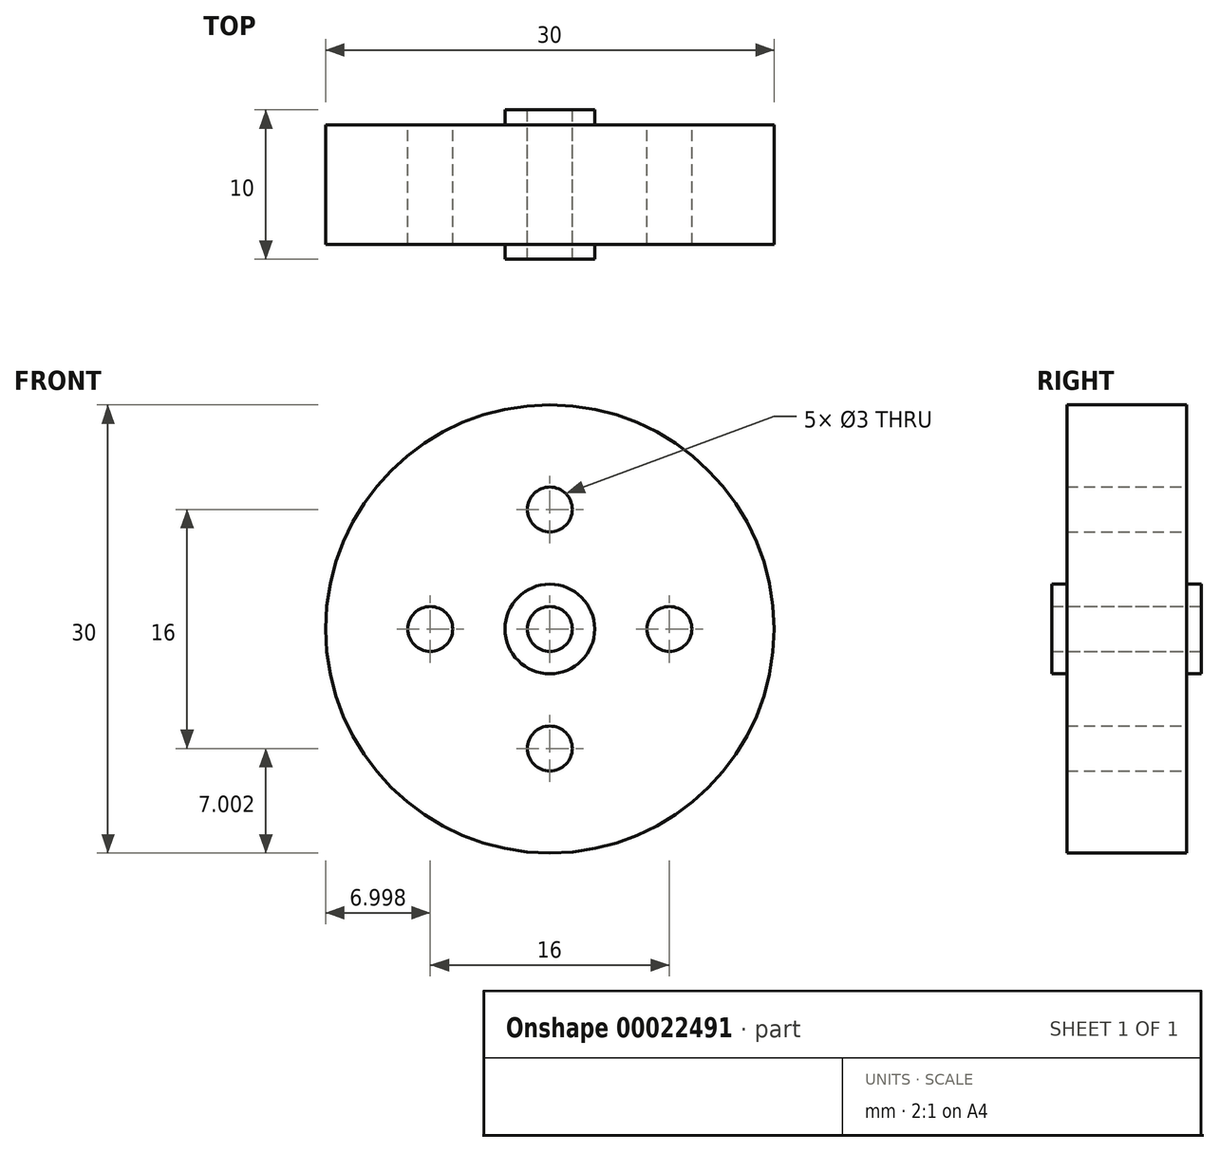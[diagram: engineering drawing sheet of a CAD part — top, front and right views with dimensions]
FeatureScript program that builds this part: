
annotation { "Feature Type Name" : "Feature", "Feature Type Description" : "" }
export const myFeature = defineFeature(function(context is Context, id is Id, definition is map)
    precondition{}
    {
        {
            var Q0;
            Q0=qCreatedBy(makeId("Front.planeOp"),FACE);
            var sketch = newSketch(context, id + "F0", { "sketchPlane" : qUnion([Q0])});
            skCircle(sketch, "E0", {"center": v(-18.25, 12.61) * mm, "radius": 15 * mm});
            skCircle(sketch, "E1", {"center": v(-18.25, 12.61) * mm, "radius": 1.5 * mm});
            skCircle(sketch, "E2", {"center": v(-18.25, 12.61) * mm, "radius": 3.5 * mm});
            skLineSegment(sketch, "E3", {"start": v(-18.25, 12.61) * mm, "end": v(-18.25, 27.61) * mm});
            skCircle(sketch, "E4", {"center": v(-18.25, 20.61) * mm, "radius": 1.5 * mm});
            skCircle(sketch, "E5.1.0", {"center": v(-26.25, 12.61) * mm, "radius": 1.5 * mm});
            skCircle(sketch, "E5.2.0", {"center": v(-18.25, 4.61) * mm, "radius": 1.5 * mm});
            skCircle(sketch, "E5.3.0", {"center": v(-10.25, 12.61) * mm, "radius": 1.5 * mm});
            skSolve(sketch);
        }
        {
            var Q0;
            Q0=makeQuery(id+"F0.imprint","IMPRINT",FACE,{"disambiguationData":[TD([[makeQuery(id+"F0.imprint","IMPRINT",EDGE,{"derivedFrom":sQuery(id+"F0.wireOp",EDGE,"E0")}),1.0]])]});
            var Q1;
            Q1=makeQuery(id+"F0.imprint","IMPRINT",FACE,{"disambiguationData":[TD([[makeQuery(id+"F0.imprint","IMPRINT",EDGE,{"derivedFrom":sQuery(id+"F0.wireOp",EDGE,"E1")}),-1.0]])]});
            extrude(context, id + "F1", {"entities" : qUnion([Q0, Q1]), "depth" : 8 * mm});
        }
        {
            var Q0;
            Q0=makeQuery(id+"F1.opExtrude","CAP_FACE",FACE,{"disambiguationData":[OSD([sQuery(id+"F0.wireOp",EDGE,"E0"),sQuery(id+"F0.wireOp",EDGE,"E1")])],"isStart":true});
            var sketch = newSketch(context, id + "F2", { "sketchPlane" : qUnion([Q0])});
            skCircle(sketch, "E6", {"center": v(18.25, 12.61) * mm, "radius": 3 * mm});
            skSolve(sketch);
        }
        {
            var Q0;
            Q0=makeQuery(id+"F2.imprint","IMPRINT",FACE,{"disambiguationData":[TD([[makeQuery(id+"F2.imprint","IMPRINT",EDGE,{"derivedFrom":sQuery(id+"F2.wireOp",EDGE,"E6")}),1.0]])]});
            extrude(context, id + "F3", {"entities" : qUnion([Q0]), "operationType" : NewBodyOperationType.ADD, "depth" : 1 * mm});
        }
        {
            var Q0;
            Q0=makeQuery(id+"F1.opExtrude","CAP_FACE",FACE,{"disambiguationData":[OSD([sQuery(id+"F0.wireOp",EDGE,"E0"),sQuery(id+"F0.wireOp",EDGE,"E1")])],"isStart":false});
            var sketch = newSketch(context, id + "F4", { "sketchPlane" : qUnion([Q0])});
            skCircle(sketch, "E7", {"center": v(-18.25, 12.61) * mm, "radius": 3 * mm});
            skSolve(sketch);
        }
        {
            var Q0;
            Q0=makeQuery(id+"F4.imprint","IMPRINT",FACE,{"disambiguationData":[TD([[makeQuery(id+"F4.imprint","IMPRINT",EDGE,{"derivedFrom":sQuery(id+"F4.wireOp",EDGE,"E7")}),1.0]])]});
            extrude(context, id + "F5", {"entities" : qUnion([Q0]), "operationType" : NewBodyOperationType.ADD, "depth" : 1 * mm});
        }
    });
